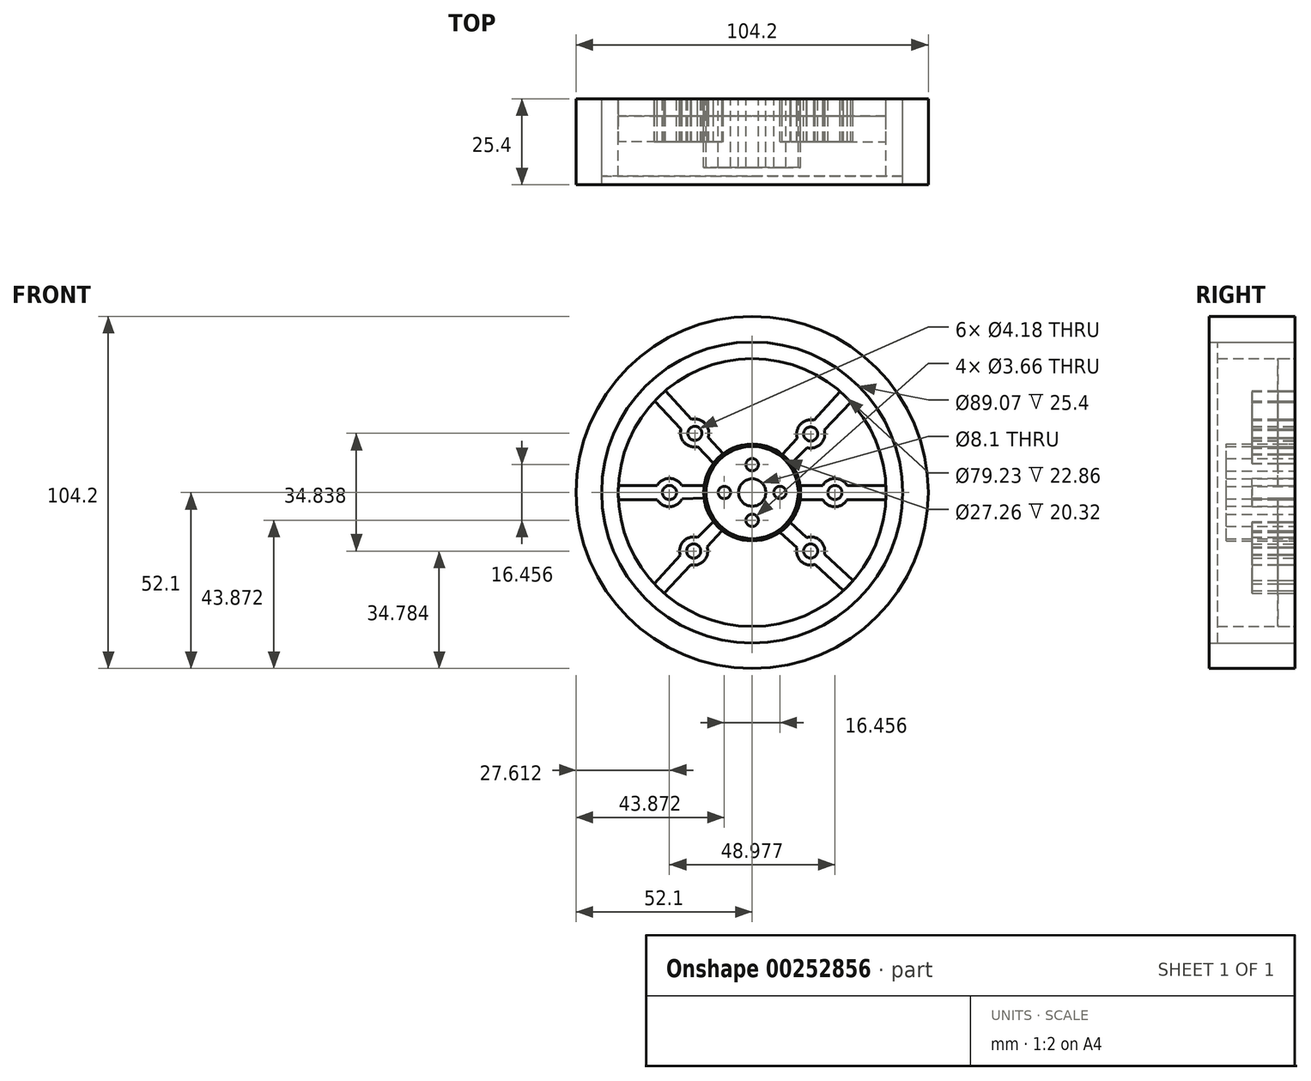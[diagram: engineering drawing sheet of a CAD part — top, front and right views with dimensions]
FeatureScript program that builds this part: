
annotation { "Feature Type Name" : "Feature", "Feature Type Description" : "" }
export const myFeature = defineFeature(function(context is Context, id is Id, definition is map)
    precondition{}
    {
        {
            var Q0;
            Q0=qCreatedBy(makeId("Front.planeOp"),FACE);
            var sketch = newSketch(context, id + "F0", { "sketchPlane" : qUnion([Q0])});
            skCircle(sketch, "E0", {"center": v(0, 0) * mm, "radius": 52.24 * mm});
            skCircle(sketch, "E1", {"center": v(0, 0) * mm, "radius": 4.05 * mm});
            skCircle(sketch, "E2", {"center": v(0, 0) * mm, "radius": 8.23 * mm});
            skCircle(sketch, "E3", {"center": v(0, 0) * mm, "radius": 13.06 * mm});
            skCircle(sketch, "E4", {"center": v(0, -8.23) * mm, "radius": 1.83 * mm});
            skCircle(sketch, "E5", {"center": v(8.23, 0) * mm, "radius": 1.83 * mm});
            skCircle(sketch, "E6", {"center": v(0, 8.23) * mm, "radius": 1.83 * mm});
            skCircle(sketch, "E7", {"center": v(-8.23, 0) * mm, "radius": 1.83 * mm});
            skCircle(sketch, "E8", {"center": v(0, 0) * mm, "radius": 14.34 * mm});
            skCircle(sketch, "E9", {"center": v(0, 0) * mm, "radius": 13.63 * mm});
            skCircle(sketch, "E10", {"center": v(24.49, 0) * mm, "radius": 2.09 * mm});
            skCircle(sketch, "E11", {"center": v(-24.49, 0) * mm, "radius": 2.09 * mm});
            skCircle(sketch, "E12", {"center": v(17.32, 17.32) * mm, "radius": 2.09 * mm});
            skCircle(sketch, "E13", {"center": v(17.32, -17.32) * mm, "radius": 2.09 * mm});
            skCircle(sketch, "E14", {"center": v(-17.32, -17.32) * mm, "radius": 2.09 * mm});
            skLineSegment(sketch, "E15", {"start": v(20.87, 2.09) * mm, "end": v(14.18, 2.09) * mm});
            skLineSegment(sketch, "E16", {"start": v(20.87, -2.09) * mm, "end": v(14.18, -2.09) * mm});
            skArc(sketch, "E17", {"start": v(28.1, 2.09) * mm, "mid": v(24.49, 4.16) * mm, "end": v(20.87, 2.09) * mm});
            skArc(sketch, "E18", {"start": v(20.87, -2.09) * mm, "mid": v(24.49, -4.2) * mm, "end": v(28.1, -2.09) * mm});
            skLineSegment(sketch, "E19", {"start": v(-20.87, 2.09) * mm, "end": v(-14.18, 2.09) * mm});
            skLineSegment(sketch, "E20", {"start": v(-20.78, -1.93) * mm, "end": v(-14.24, -1.65) * mm});
            skArc(sketch, "E21", {"start": v(-20.87, 2.09) * mm, "mid": v(-24.49, 4.19) * mm, "end": v(-28.1, 2.09) * mm});
            skArc(sketch, "E22", {"start": v(-28.1, -2.09) * mm, "mid": v(-24.4, -4.18) * mm, "end": v(-20.78, -1.93) * mm});
            skLineSegment(sketch, "E23", {"start": v(13.33, 16.06) * mm, "end": v(8.9, 11.24) * mm});
            skLineSegment(sketch, "E24", {"start": v(16.25, 13.27) * mm, "end": v(11.54, 8.5) * mm});
            skArc(sketch, "E25", {"start": v(18.22, 21.4) * mm, "mid": v(14.24, 20.14) * mm, "end": v(13.33, 16.06) * mm});
            skArc(sketch, "E26", {"start": v(16.25, 13.27) * mm, "mid": v(20.31, 14.4) * mm, "end": v(21.33, 18.49) * mm});
            skLineSegment(sketch, "E27", {"start": v(-13.33, -16.06) * mm, "end": v(-8.9, -11.24) * mm});
            skLineSegment(sketch, "E28", {"start": v(-16.2, -13.29) * mm, "end": v(-11.46, -8.61) * mm});
            skArc(sketch, "E29", {"start": v(-18.22, -21.4) * mm, "mid": v(-14.23, -20.15) * mm, "end": v(-13.33, -16.06) * mm});
            skArc(sketch, "E30", {"start": v(-16.2, -13.29) * mm, "mid": v(-20.32, -14.42) * mm, "end": v(-21.3, -18.58) * mm});
            skLineSegment(sketch, "E31", {"start": v(16.06, -13.33) * mm, "end": v(11.24, -8.9) * mm});
            skLineSegment(sketch, "E32", {"start": v(13.24, -16.4) * mm, "end": v(8.2, -11.76) * mm});
            skArc(sketch, "E33", {"start": v(21.4, -18.22) * mm, "mid": v(20.13, -14.25) * mm, "end": v(16.06, -13.33) * mm});
            skArc(sketch, "E34", {"start": v(13.24, -16.4) * mm, "mid": v(14.5, -20.38) * mm, "end": v(18.58, -21.3) * mm});
            skCircle(sketch, "E35", {"center": v(0, 0) * mm, "radius": 39.61 * mm});
            skCircle(sketch, "E36", {"center": v(0, 0) * mm, "radius": 44.53 * mm});
            skCircle(sketch, "E37", {"center": v(0, 0) * mm, "radius": 52.1 * mm});
            skLineSegment(sketch, "E38", {"start": v(26.01, 29.88) * mm, "end": v(18.22, 21.4) * mm});
            skLineSegment(sketch, "E39", {"start": v(29.24, 26.73) * mm, "end": v(21.33, 18.49) * mm});
            skLineSegment(sketch, "E40", {"start": v(39.56, 2.09) * mm, "end": v(28.1, 2.09) * mm});
            skLineSegment(sketch, "E41", {"start": v(39.56, -2.09) * mm, "end": v(28.1, -2.09) * mm});
            skLineSegment(sketch, "E42", {"start": v(29.88, -26.01) * mm, "end": v(21.4, -18.22) * mm});
            skLineSegment(sketch, "E43", {"start": v(26.98, -29.01) * mm, "end": v(18.58, -21.3) * mm});
            skLineSegment(sketch, "E44", {"start": v(-29.01, -26.98) * mm, "end": v(-21.3, -18.58) * mm});
            skLineSegment(sketch, "E45", {"start": v(-26.01, -29.88) * mm, "end": v(-18.22, -21.4) * mm});
            skLineSegment(sketch, "E46", {"start": v(-39.56, 2.09) * mm, "end": v(-28.1, 2.09) * mm});
            skLineSegment(sketch, "E47", {"start": v(-39.56, -2.09) * mm, "end": v(-28.1, -2.09) * mm});
            skLineSegment(sketch, "E48.0.1", {"start": v(-8.58, 11.48) * mm, "end": v(-13.01, 16.3) * mm});
            skArc(sketch, "E48.0.2", {"start": v(-13.01, 16.3) * mm, "mid": v(-13.92, 20.4) * mm, "end": v(-17.92, 21.66) * mm});
            skLineSegment(sketch, "E48.0.3", {"start": v(-17.92, 21.66) * mm, "end": v(-25.7, 30.14) * mm});
            skLineSegment(sketch, "E48.0.5", {"start": v(-28.92, 27.07) * mm, "end": v(-21.06, 18.8) * mm});
            skArc(sketch, "E48.0.6", {"start": v(-21.06, 18.8) * mm, "mid": v(-20.08, 14.76) * mm, "end": v(-16.1, 13.57) * mm});
            skLineSegment(sketch, "E48.0.7", {"start": v(-16.1, 13.57) * mm, "end": v(-11.43, 8.65) * mm});
            skCircle(sketch, "E49.0", {"center": v(-16.97, 17.52) * mm, "radius": 2.09 * mm});
            skLineSegment(sketch, "E50", {"start": v(-13.01, 16.3) * mm, "end": v(-8.58, 11.48) * mm});
            skArc(sketch, "E51", {"start": v(-21.06, 18.8) * mm, "mid": v(-20.09, 14.75) * mm, "end": v(-16.1, 13.57) * mm});
            skSolve(sketch);
        }
        {
            var Q0;
            Q0=qCreatedBy(makeId("Front.planeOp"),FACE);
            var sketch = newSketch(context, id + "F1", { "sketchPlane" : qUnion([Q0])});
            skArc(sketch, "E52.0.0", {"start": v(8.9, 11.24) * mm, "mid": v(10.3, 9.96) * mm, "end": v(11.54, 8.5) * mm});
            skLineSegment(sketch, "E52.0.1", {"start": v(11.54, 8.5) * mm, "end": v(16.25, 13.27) * mm});
            skArc(sketch, "E52.0.2", {"start": v(16.25, 13.27) * mm, "mid": v(20.31, 14.4) * mm, "end": v(21.33, 18.49) * mm});
            skLineSegment(sketch, "E52.0.3", {"start": v(21.33, 18.49) * mm, "end": v(29.24, 26.73) * mm});
            skArc(sketch, "E52.0.4", {"start": v(29.24, 26.73) * mm, "mid": v(27.67, 28.35) * mm, "end": v(26.01, 29.88) * mm});
            skLineSegment(sketch, "E52.0.5", {"start": v(26.01, 29.88) * mm, "end": v(18.22, 21.4) * mm});
            skArc(sketch, "E52.0.6", {"start": v(18.22, 21.4) * mm, "mid": v(14.24, 20.14) * mm, "end": v(13.33, 16.06) * mm});
            skLineSegment(sketch, "E52.0.7", {"start": v(13.33, 16.06) * mm, "end": v(8.9, 11.24) * mm});
            skCircle(sketch, "E53.0.0", {"center": v(17.32, 17.32) * mm, "radius": 2.09 * mm});
            skArc(sketch, "E54.0.0", {"start": v(39.56, -2.09) * mm, "mid": v(39.61, 0) * mm, "end": v(39.56, 2.09) * mm});
            skLineSegment(sketch, "E54.0.1", {"start": v(39.56, 2.09) * mm, "end": v(28.1, 2.09) * mm});
            skArc(sketch, "E54.0.2", {"start": v(28.1, 2.09) * mm, "mid": v(24.49, 4.16) * mm, "end": v(20.87, 2.09) * mm});
            skLineSegment(sketch, "E54.0.3", {"start": v(20.87, 2.09) * mm, "end": v(14.18, 2.09) * mm});
            skArc(sketch, "E54.0.4", {"start": v(14.18, 2.09) * mm, "mid": v(14.34, 0) * mm, "end": v(14.18, -2.09) * mm});
            skLineSegment(sketch, "E54.0.5", {"start": v(14.18, -2.09) * mm, "end": v(20.87, -2.09) * mm});
            skArc(sketch, "E54.0.6", {"start": v(20.87, -2.09) * mm, "mid": v(24.49, -4.2) * mm, "end": v(28.1, -2.09) * mm});
            skLineSegment(sketch, "E54.0.7", {"start": v(28.1, -2.09) * mm, "end": v(39.56, -2.09) * mm});
            skCircle(sketch, "E54.1.0", {"center": v(24.49, 0) * mm, "radius": 2.09 * mm});
            skLineSegment(sketch, "E55.0.0", {"start": v(18.58, -21.3) * mm, "end": v(26.98, -29.01) * mm});
            skArc(sketch, "E55.0.1", {"start": v(26.98, -29.01) * mm, "mid": v(28.47, -27.55) * mm, "end": v(29.88, -26.01) * mm});
            skLineSegment(sketch, "E55.0.2", {"start": v(29.88, -26.01) * mm, "end": v(21.4, -18.22) * mm});
            skArc(sketch, "E55.0.3", {"start": v(21.4, -18.22) * mm, "mid": v(20.13, -14.25) * mm, "end": v(16.06, -13.33) * mm});
            skLineSegment(sketch, "E55.0.4", {"start": v(16.06, -13.33) * mm, "end": v(11.24, -8.9) * mm});
            skArc(sketch, "E55.0.5", {"start": v(11.24, -8.9) * mm, "mid": v(9.82, -10.44) * mm, "end": v(8.2, -11.76) * mm});
            skLineSegment(sketch, "E55.0.6", {"start": v(8.2, -11.76) * mm, "end": v(13.24, -16.4) * mm});
            skArc(sketch, "E55.0.7", {"start": v(13.24, -16.4) * mm, "mid": v(14.5, -20.38) * mm, "end": v(18.58, -21.3) * mm});
            skCircle(sketch, "E55.1.0", {"center": v(17.32, -17.32) * mm, "radius": 2.09 * mm});
            skLineSegment(sketch, "E56.0.0", {"start": v(-21.3, -18.58) * mm, "end": v(-29.01, -26.98) * mm});
            skArc(sketch, "E56.0.1", {"start": v(-29.01, -26.98) * mm, "mid": v(-27.55, -28.47) * mm, "end": v(-26.01, -29.88) * mm});
            skLineSegment(sketch, "E56.0.2", {"start": v(-26.01, -29.88) * mm, "end": v(-18.22, -21.4) * mm});
            skArc(sketch, "E56.0.3", {"start": v(-18.22, -21.4) * mm, "mid": v(-14.23, -20.15) * mm, "end": v(-13.33, -16.06) * mm});
            skLineSegment(sketch, "E56.0.4", {"start": v(-13.33, -16.06) * mm, "end": v(-8.9, -11.24) * mm});
            skArc(sketch, "E56.0.5", {"start": v(-8.9, -11.24) * mm, "mid": v(-10.26, -10) * mm, "end": v(-11.46, -8.61) * mm});
            skLineSegment(sketch, "E56.0.6", {"start": v(-11.46, -8.61) * mm, "end": v(-16.2, -13.29) * mm});
            skArc(sketch, "E56.0.7", {"start": v(-16.2, -13.29) * mm, "mid": v(-20.32, -14.42) * mm, "end": v(-21.3, -18.58) * mm});
            skCircle(sketch, "E56.1.0", {"center": v(-17.32, -17.32) * mm, "radius": 2.09 * mm});
            skArc(sketch, "E57.0.0", {"start": v(-39.56, 2.09) * mm, "mid": v(-39.61, 0) * mm, "end": v(-39.56, -2.09) * mm});
            skLineSegment(sketch, "E57.0.1", {"start": v(-39.56, -2.09) * mm, "end": v(-28.1, -2.09) * mm});
            skArc(sketch, "E57.0.2", {"start": v(-28.1, -2.09) * mm, "mid": v(-24.4, -4.18) * mm, "end": v(-20.78, -1.93) * mm});
            skLineSegment(sketch, "E57.0.3", {"start": v(-20.78, -1.93) * mm, "end": v(-14.24, -1.65) * mm});
            skArc(sketch, "E57.0.4", {"start": v(-14.24, -1.65) * mm, "mid": v(-14.33, 0.22) * mm, "end": v(-14.18, 2.09) * mm});
            skLineSegment(sketch, "E57.0.5", {"start": v(-14.18, 2.09) * mm, "end": v(-20.87, 2.09) * mm});
            skArc(sketch, "E57.0.6", {"start": v(-20.87, 2.09) * mm, "mid": v(-24.49, 4.19) * mm, "end": v(-28.1, 2.09) * mm});
            skLineSegment(sketch, "E57.0.7", {"start": v(-28.1, 2.09) * mm, "end": v(-39.56, 2.09) * mm});
            skCircle(sketch, "E57.1.0", {"center": v(-24.49, 0) * mm, "radius": 2.09 * mm});
            skArc(sketch, "E58.0.0", {"start": v(-11.43, 8.65) * mm, "mid": v(-10.1, 10.17) * mm, "end": v(-8.58, 11.48) * mm});
            skLineSegment(sketch, "E58.0.1", {"start": v(-8.58, 11.48) * mm, "end": v(-13.01, 16.3) * mm});
            skArc(sketch, "E58.0.2", {"start": v(-13.01, 16.3) * mm, "mid": v(-13.92, 20.4) * mm, "end": v(-17.92, 21.66) * mm});
            skLineSegment(sketch, "E58.0.3", {"start": v(-17.92, 21.66) * mm, "end": v(-25.7, 30.14) * mm});
            skArc(sketch, "E58.0.4", {"start": v(-25.7, 30.14) * mm, "mid": v(-27.36, 28.65) * mm, "end": v(-28.92, 27.07) * mm});
            skLineSegment(sketch, "E58.0.5", {"start": v(-28.92, 27.07) * mm, "end": v(-21.06, 18.8) * mm});
            skArc(sketch, "E58.0.6", {"start": v(-21.06, 18.8) * mm, "mid": v(-20.08, 14.76) * mm, "end": v(-16.1, 13.57) * mm});
            skLineSegment(sketch, "E58.0.7", {"start": v(-16.1, 13.57) * mm, "end": v(-11.43, 8.65) * mm});
            skCircle(sketch, "E59.0.0", {"center": v(-16.97, 17.52) * mm, "radius": 2.09 * mm});
            skSolve(sketch);
        }
        {
            var Q0;
            Q0=makeQuery(id+"F0.imprint","IMPRINT",FACE,{"disambiguationData":[TD([[makeQuery(id+"F0.imprint","IMPRINT",EDGE,{"derivedFrom":sQuery(id+"F0.wireOp",EDGE,"E9")}),-1.0]])]});
            var sketch = newSketch(context, id + "F2", { "sketchPlane" : qUnion([Q0])});
            skCircle(sketch, "E60.0", {"center": v(0, 0) * mm, "radius": 14.34 * mm});
            skCircle(sketch, "E61.0", {"center": v(-8.23, 0) * mm, "radius": 1.83 * mm});
            skCircle(sketch, "E62.0", {"center": v(0, 8.23) * mm, "radius": 1.83 * mm});
            skCircle(sketch, "E63.0", {"center": v(0, -8.23) * mm, "radius": 1.83 * mm});
            skCircle(sketch, "E64.0", {"center": v(8.23, 0) * mm, "radius": 1.83 * mm});
            skCircle(sketch, "E65.0", {"center": v(0, 0) * mm, "radius": 4.05 * mm});
            skSolve(sketch);
        }
        {
            var Q0;
            Q0=qCreatedBy(makeId("Front.planeOp"),FACE);
            var sketch = newSketch(context, id + "F3", { "sketchPlane" : qUnion([Q0])});
            skLineSegment(sketch, "E66.0.0", {"start": v(-21.06, 18.8) * mm, "end": v(-28.92, 27.07) * mm});
            skArc(sketch, "E66.0.1", {"start": v(-28.92, 27.07) * mm, "mid": v(-36.45, 15.52) * mm, "end": v(-39.56, 2.09) * mm});
            skLineSegment(sketch, "E66.0.2", {"start": v(-39.56, 2.09) * mm, "end": v(-28.1, 2.09) * mm});
            skArc(sketch, "E66.0.3", {"start": v(-28.1, 2.09) * mm, "mid": v(-24.49, 4.19) * mm, "end": v(-20.87, 2.09) * mm});
            skLineSegment(sketch, "E66.0.4", {"start": v(-20.87, 2.09) * mm, "end": v(-14.18, 2.09) * mm});
            skArc(sketch, "E66.0.5", {"start": v(-14.18, 2.09) * mm, "mid": v(-13.22, 5.54) * mm, "end": v(-11.43, 8.65) * mm});
            skLineSegment(sketch, "E66.0.6", {"start": v(-11.43, 8.65) * mm, "end": v(-16.1, 13.57) * mm});
            skArc(sketch, "E66.0.7", {"start": v(-16.1, 13.57) * mm, "mid": v(-20.09, 14.75) * mm, "end": v(-21.06, 18.8) * mm});
            skLineSegment(sketch, "E67.0.0", {"start": v(18.22, 21.4) * mm, "end": v(26.01, 29.88) * mm});
            skArc(sketch, "E67.0.1", {"start": v(26.01, 29.88) * mm, "mid": v(0.2, 39.61) * mm, "end": v(-25.7, 30.14) * mm});
            skLineSegment(sketch, "E67.0.2", {"start": v(-25.7, 30.14) * mm, "end": v(-17.92, 21.66) * mm});
            skArc(sketch, "E67.0.3", {"start": v(-17.92, 21.66) * mm, "mid": v(-13.92, 20.4) * mm, "end": v(-13.01, 16.3) * mm});
            skLineSegment(sketch, "E67.0.4", {"start": v(-13.01, 16.3) * mm, "end": v(-8.58, 11.48) * mm});
            skArc(sketch, "E67.0.5", {"start": v(-8.58, 11.48) * mm, "mid": v(0.2, 14.33) * mm, "end": v(8.9, 11.24) * mm});
            skLineSegment(sketch, "E67.0.6", {"start": v(8.9, 11.24) * mm, "end": v(13.33, 16.06) * mm});
            skArc(sketch, "E67.0.7", {"start": v(13.33, 16.06) * mm, "mid": v(14.24, 20.14) * mm, "end": v(18.22, 21.4) * mm});
            skArc(sketch, "E68.0.0", {"start": v(39.56, 2.09) * mm, "mid": v(36.54, 15.3) * mm, "end": v(29.24, 26.73) * mm});
            skLineSegment(sketch, "E68.0.1", {"start": v(29.24, 26.73) * mm, "end": v(21.33, 18.49) * mm});
            skArc(sketch, "E68.0.2", {"start": v(21.33, 18.49) * mm, "mid": v(20.31, 14.4) * mm, "end": v(16.25, 13.27) * mm});
            skLineSegment(sketch, "E68.0.3", {"start": v(16.25, 13.27) * mm, "end": v(11.54, 8.5) * mm});
            skArc(sketch, "E68.0.4", {"start": v(11.54, 8.5) * mm, "mid": v(13.25, 5.46) * mm, "end": v(14.18, 2.09) * mm});
            skLineSegment(sketch, "E68.0.5", {"start": v(14.18, 2.09) * mm, "end": v(20.87, 2.09) * mm});
            skArc(sketch, "E68.0.6", {"start": v(20.87, 2.09) * mm, "mid": v(24.49, 4.16) * mm, "end": v(28.1, 2.09) * mm});
            skLineSegment(sketch, "E68.0.7", {"start": v(28.1, 2.09) * mm, "end": v(39.56, 2.09) * mm});
            skLineSegment(sketch, "E69.0.0", {"start": v(21.4, -18.22) * mm, "end": v(29.88, -26.01) * mm});
            skArc(sketch, "E69.0.1", {"start": v(29.88, -26.01) * mm, "mid": v(36.72, -14.86) * mm, "end": v(39.56, -2.09) * mm});
            skLineSegment(sketch, "E69.0.2", {"start": v(39.56, -2.09) * mm, "end": v(28.1, -2.09) * mm});
            skArc(sketch, "E69.0.3", {"start": v(28.1, -2.09) * mm, "mid": v(24.49, -4.2) * mm, "end": v(20.87, -2.09) * mm});
            skLineSegment(sketch, "E69.0.4", {"start": v(20.87, -2.09) * mm, "end": v(14.18, -2.09) * mm});
            skArc(sketch, "E69.0.5", {"start": v(14.18, -2.09) * mm, "mid": v(13.16, -5.69) * mm, "end": v(11.24, -8.9) * mm});
            skLineSegment(sketch, "E69.0.6", {"start": v(11.24, -8.9) * mm, "end": v(16.06, -13.33) * mm});
            skArc(sketch, "E69.0.7", {"start": v(16.06, -13.33) * mm, "mid": v(20.13, -14.25) * mm, "end": v(21.4, -18.22) * mm});
            skLineSegment(sketch, "E70.0.0", {"start": v(-18.22, -21.4) * mm, "end": v(-26.01, -29.88) * mm});
            skArc(sketch, "E70.0.1", {"start": v(-26.01, -29.88) * mm, "mid": v(0.65, -39.6) * mm, "end": v(26.98, -29.01) * mm});
            skLineSegment(sketch, "E70.0.2", {"start": v(26.98, -29.01) * mm, "end": v(18.58, -21.3) * mm});
            skArc(sketch, "E70.0.3", {"start": v(18.58, -21.3) * mm, "mid": v(14.5, -20.38) * mm, "end": v(13.24, -16.4) * mm});
            skLineSegment(sketch, "E70.0.4", {"start": v(13.24, -16.4) * mm, "end": v(8.2, -11.76) * mm});
            skArc(sketch, "E70.0.5", {"start": v(8.2, -11.76) * mm, "mid": v(-0.44, -14.33) * mm, "end": v(-8.9, -11.24) * mm});
            skLineSegment(sketch, "E70.0.6", {"start": v(-8.9, -11.24) * mm, "end": v(-13.33, -16.06) * mm});
            skArc(sketch, "E70.0.7", {"start": v(-13.33, -16.06) * mm, "mid": v(-14.23, -20.15) * mm, "end": v(-18.22, -21.4) * mm});
            skLineSegment(sketch, "E71.0.0", {"start": v(-28.1, -2.09) * mm, "end": v(-39.56, -2.09) * mm});
            skArc(sketch, "E71.0.1", {"start": v(-39.56, -2.09) * mm, "mid": v(-36.47, -15.46) * mm, "end": v(-29.01, -26.98) * mm});
            skLineSegment(sketch, "E71.0.2", {"start": v(-29.01, -26.98) * mm, "end": v(-21.3, -18.58) * mm});
            skArc(sketch, "E71.0.3", {"start": v(-21.3, -18.58) * mm, "mid": v(-20.32, -14.42) * mm, "end": v(-16.2, -13.29) * mm});
            skLineSegment(sketch, "E71.0.4", {"start": v(-16.2, -13.29) * mm, "end": v(-11.46, -8.61) * mm});
            skArc(sketch, "E71.0.5", {"start": v(-11.46, -8.61) * mm, "mid": v(-13.31, -5.32) * mm, "end": v(-14.24, -1.65) * mm});
            skLineSegment(sketch, "E71.0.6", {"start": v(-14.24, -1.65) * mm, "end": v(-20.78, -1.93) * mm});
            skArc(sketch, "E71.0.7", {"start": v(-20.78, -1.93) * mm, "mid": v(-24.4, -4.18) * mm, "end": v(-28.1, -2.09) * mm});
            skSolve(sketch);
        }
        {
            var Q0;
            Q0=makeQuery(id+"F0.imprint","IMPRINT",FACE,{"disambiguationData":[TD([[makeQuery(id+"F0.imprint","IMPRINT",EDGE,{"derivedFrom":sQuery(id+"F0.wireOp",EDGE,"E36")}),-1.0]])]});
            extrude(context, id + "F4", {"entities" : qUnion([Q0]), "depth" : 25.4 * mm});
        }
        {
            var Q0;
            Q0 = qSketchRegion(id + "F1", true);
            extrude(context, id + "F5", {"entities" : qUnion([Q0]), "depth" : 12.7 * mm});
        }
        {
            var Q0;
            Q0=makeQuery(id+"F2.imprint","IMPRINT",FACE,{"disambiguationData":[TD([[makeQuery(id+"F2.imprint","IMPRINT",EDGE,{"derivedFrom":sQuery(id+"F2.wireOp",EDGE,"E61.0")}),-1.0]])]});
            var Q1;
            Q1=makeQuery(id+"F0.imprint","IMPRINT",FACE,{"disambiguationData":[TD([[makeQuery(id+"F0.imprint","IMPRINT",EDGE,{"derivedFrom":sQuery(id+"F0.wireOp",EDGE,"E9")}),-1.0]])]});
            extrude(context, id + "F6", {"entities" : qUnion([Q0, Q1]), "depth" : 20.32 * mm});
        }
        {
            var Q0;
            Q0 = qSketchRegion(id + "F3", true);
            extrude(context, id + "F7", {"entities" : qUnion([Q0]), "depth" : 5.08 * mm});
        }
        {
            var Q0;
            Q0=makeQuery(id+"F0.imprint","IMPRINT",FACE,{"disambiguationData":[TD([[makeQuery(id+"F0.imprint","IMPRINT",EDGE,{"derivedFrom":sQuery(id+"F0.wireOp",EDGE,"E36")}),1.0]])]});
            var sketch = newSketch(context, id + "F8", { "sketchPlane" : qUnion([Q0])});
            skCircle(sketch, "E72.0.0", {"center": v(0, 0) * mm, "radius": 44.53 * mm});
            skSolve(sketch);
        }
        {
            var Q0;
            Q0=makeQuery(id+"F8.imprint","IMPRINT",FACE,{"disambiguationData":[TD([[makeQuery(id+"F8.imprint","IMPRINT",EDGE,{"derivedFrom":sQuery(id+"F8.wireOp",EDGE,"E72.0.0")}),1.0]])]});
            extrude(context, id + "F9", {"entities" : qUnion([Q0]), "depth" : 22.86 * mm});
        }
    });
